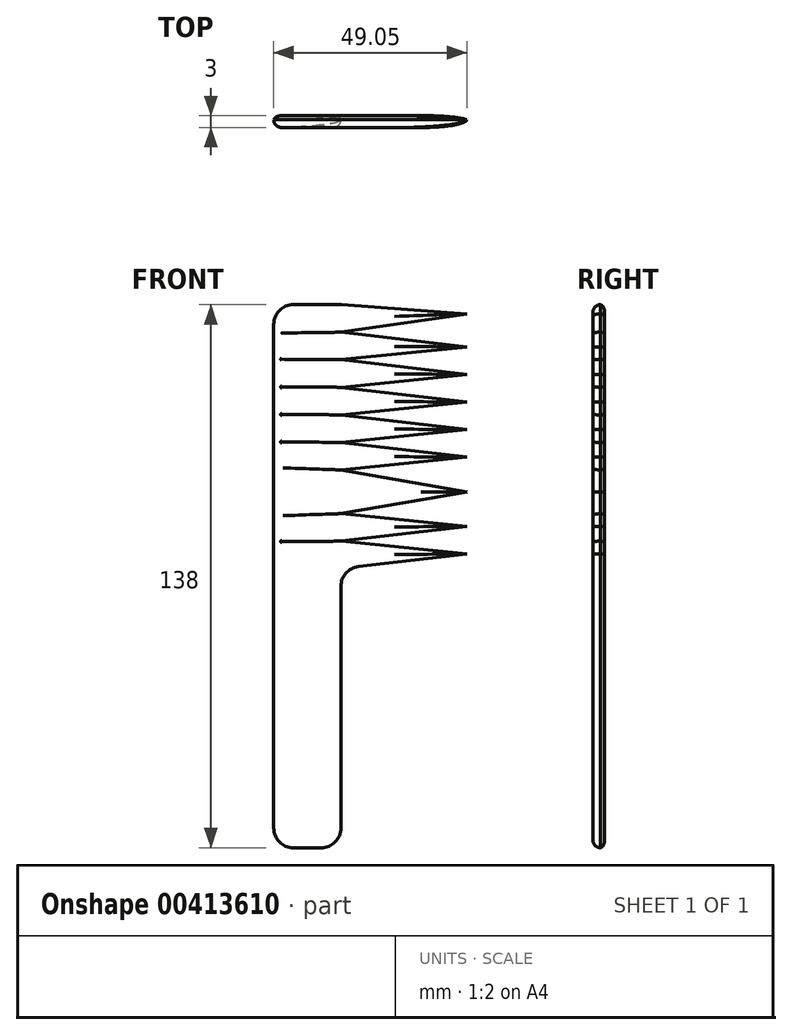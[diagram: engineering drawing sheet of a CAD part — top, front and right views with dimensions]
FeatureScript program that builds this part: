
annotation { "Feature Type Name" : "Feature", "Feature Type Description" : "" }
export const myFeature = defineFeature(function(context is Context, id is Id, definition is map)
    precondition{}
    {
        {
            var Q0;
            Q0=qCreatedBy(makeId("Front.planeOp"),FACE);
            var sketch = newSketch(context, id + "F0", { "sketchPlane" : qUnion([Q0])});
            skLineSegment(sketch, "E0", {"start": v(-43.23, 59.14) * mm, "end": v(-55.11, 59.14) * mm});
            skLineSegment(sketch, "E1", {"start": v(-60.11, 54.14) * mm, "end": v(-60.11, -73.86) * mm});
            skLineSegment(sketch, "E2", {"start": v(-55.11, -78.86) * mm, "end": v(-48.05, -78.86) * mm});
            skLineSegment(sketch, "E3", {"start": v(-43.05, -73.86) * mm, "end": v(-43.05, -12.4) * mm});
            skLineSegment(sketch, "E4", {"start": v(-11.06, 11.6) * mm, "end": v(-43.05, 17.14) * mm});
            skLineSegment(sketch, "E5", {"start": v(-43.05, 17.14) * mm, "end": v(-11.06, 20.38) * mm});
            skLineSegment(sketch, "E6", {"start": v(-11.06, 20.38) * mm, "end": v(-43.05, 24.14) * mm});
            skLineSegment(sketch, "E7", {"start": v(-43.05, 24.14) * mm, "end": v(-11.06, 27.38) * mm});
            skLineSegment(sketch, "E8", {"start": v(-11.06, 27.38) * mm, "end": v(-43.05, 31.14) * mm});
            skLineSegment(sketch, "E9", {"start": v(-43.05, 31.14) * mm, "end": v(-11.06, 34.38) * mm});
            skLineSegment(sketch, "E10", {"start": v(-11.06, 34.38) * mm, "end": v(-43.05, 38.14) * mm});
            skLineSegment(sketch, "E11", {"start": v(-43.05, 38.14) * mm, "end": v(-11.06, 41.38) * mm});
            skLineSegment(sketch, "E12", {"start": v(-11.06, 41.38) * mm, "end": v(-43.05, 45.14) * mm});
            skLineSegment(sketch, "E13", {"start": v(-43.05, 45.14) * mm, "end": v(-11.06, 48.38) * mm});
            skLineSegment(sketch, "E14", {"start": v(-11.06, 48.38) * mm, "end": v(-43.05, 52.14) * mm});
            skLineSegment(sketch, "E15", {"start": v(-43.05, 52.14) * mm, "end": v(-11.06, 56.81) * mm});
            skLineSegment(sketch, "E16", {"start": v(-11.06, 56.81) * mm, "end": v(-42.87, 59.13) * mm});
            skLineSegment(sketch, "E17.MirrorCS", {"start": v(-11.06, 11.6) * mm, "end": v(-43.05, 6.05) * mm});
            skLineSegment(sketch, "E18.MirrorCS", {"start": v(-11.06, 2.8) * mm, "end": v(-43.05, -0.95) * mm});
            skLineSegment(sketch, "E19.MirrorCS", {"start": v(-43.05, 6.05) * mm, "end": v(-11.06, 2.8) * mm});
            skLineSegment(sketch, "E20.MirrorCS", {"start": v(-43.05, -0.95) * mm, "end": v(-11.06, -4.2) * mm});
            skLineSegment(sketch, "E21.MirrorCS", {"start": v(-11.06, -4.2) * mm, "end": v(-38.63, -7.43) * mm});
            skPoint(sketch, "E22.visualSharp", {"position": v(-60.11, 59.14) * mm});
            skArc(sketch, "E22.filletArc", {"start": v(-55.11, 59.14) * mm, "mid": v(-58.65, 57.67) * mm, "end": v(-60.11, 54.14) * mm});
            skPoint(sketch, "E23.visualSharp", {"position": v(-60.11, -78.86) * mm});
            skArc(sketch, "E23.filletArc", {"start": v(-60.11, -73.86) * mm, "mid": v(-58.65, -77.4) * mm, "end": v(-55.11, -78.86) * mm});
            skPoint(sketch, "E24.visualSharp", {"position": v(-43.05, -78.86) * mm});
            skArc(sketch, "E24.filletArc", {"start": v(-48.05, -78.86) * mm, "mid": v(-44.51, -77.4) * mm, "end": v(-43.05, -73.86) * mm});
            skArc(sketch, "E25.filletArc", {"start": v(-38.63, -7.43) * mm, "mid": v(-41.79, -9.08) * mm, "end": v(-43.05, -12.4) * mm});
            skArc(sketch, "E26.filletArc", {"start": v(-42.87, 59.13) * mm, "mid": v(-43.05, 59.13) * mm, "end": v(-43.23, 59.14) * mm});
            skSolve(sketch);
        }
        {
            var Q0;
            Q0=makeQuery(id+"F0.imprint","IMPRINT",FACE,{"disambiguationData":[TD([[makeQuery(id+"F0.imprint","IMPRINT",EDGE,{"derivedFrom":sQuery(id+"F0.wireOp",EDGE,"E0")}),1.0]])]});
            extrude(context, id + "F1", {"entities" : qUnion([Q0]), "depth" : 3 * mm});
        }
        {
            var Q0;
            Q0=makeQuery(id+"F1.opExtrude","CAP_EDGE",EDGE,{"disambiguationData":[OSD([sQuery(id+"F0.wireOp",EDGE,"E1")])],"isStart":false});
            var Q1;
            Q1=makeQuery(id+"F1.opExtrude","CAP_EDGE",EDGE,{"disambiguationData":[OSD([sQuery(id+"F0.wireOp",EDGE,"E18.MirrorCS")])],"isStart":false});
            var Q2;
            Q2=makeQuery(id+"F1.opExtrude","CAP_EDGE",EDGE,{"disambiguationData":[OSD([sQuery(id+"F0.wireOp",EDGE,"E17.MirrorCS")])],"isStart":false});
            var Q3;
            Q3=makeQuery(id+"F1.opExtrude","CAP_EDGE",EDGE,{"disambiguationData":[OSD([sQuery(id+"F0.wireOp",EDGE,"E5")])],"isStart":false});
            var Q4;
            Q4=makeQuery(id+"F1.opExtrude","CAP_EDGE",EDGE,{"disambiguationData":[OSD([sQuery(id+"F0.wireOp",EDGE,"E7")])],"isStart":false});
            var Q5;
            Q5=makeQuery(id+"F1.opExtrude","CAP_EDGE",EDGE,{"disambiguationData":[OSD([sQuery(id+"F0.wireOp",EDGE,"E9")])],"isStart":false});
            var Q6;
            Q6=makeQuery(id+"F1.opExtrude","CAP_EDGE",EDGE,{"disambiguationData":[OSD([sQuery(id+"F0.wireOp",EDGE,"E11")])],"isStart":false});
            var Q7;
            Q7=makeQuery(id+"F1.opExtrude","CAP_EDGE",EDGE,{"disambiguationData":[OSD([sQuery(id+"F0.wireOp",EDGE,"E13")])],"isStart":false});
            var Q8;
            Q8=makeQuery(id+"F1.opExtrude","CAP_EDGE",EDGE,{"disambiguationData":[OSD([sQuery(id+"F0.wireOp",EDGE,"E15")])],"isStart":false});
            fillet(context, id + "F2", {"entities" : qUnion([Q0, Q1, Q2, Q3, Q4, Q5, Q6, Q7, Q8]), "radius" : 2 * mm, "tangentPropagation" : true, "allowEdgeOverflow" : false});
        }
        {
            var Q0;
            Q0=makeQuery(id+"F1.opExtrude","CAP_EDGE",EDGE,{"disambiguationData":[OSD([sQuery(id+"F0.wireOp",EDGE,"E1")])],"isStart":true});
            var Q1;
            Q1=makeQuery(id+"F1.opExtrude","CAP_EDGE",EDGE,{"disambiguationData":[OSD([sQuery(id+"F0.wireOp",EDGE,"E18.MirrorCS")])],"isStart":true});
            var Q2;
            Q2=makeQuery(id+"F1.opExtrude","CAP_EDGE",EDGE,{"disambiguationData":[OSD([sQuery(id+"F0.wireOp",EDGE,"E17.MirrorCS")])],"isStart":true});
            var Q3;
            Q3=makeQuery(id+"F1.opExtrude","CAP_EDGE",EDGE,{"disambiguationData":[OSD([sQuery(id+"F0.wireOp",EDGE,"E5")])],"isStart":true});
            var Q4;
            Q4=makeQuery(id+"F1.opExtrude","CAP_EDGE",EDGE,{"disambiguationData":[OSD([sQuery(id+"F0.wireOp",EDGE,"E7")])],"isStart":true});
            var Q5;
            Q5=makeQuery(id+"F1.opExtrude","CAP_EDGE",EDGE,{"disambiguationData":[OSD([sQuery(id+"F0.wireOp",EDGE,"E9")])],"isStart":true});
            var Q6;
            Q6=makeQuery(id+"F1.opExtrude","CAP_EDGE",EDGE,{"disambiguationData":[OSD([sQuery(id+"F0.wireOp",EDGE,"E11")])],"isStart":true});
            var Q7;
            Q7=makeQuery(id+"F1.opExtrude","CAP_EDGE",EDGE,{"disambiguationData":[OSD([sQuery(id+"F0.wireOp",EDGE,"E13")])],"isStart":true});
            var Q8;
            Q8=makeQuery(id+"F1.opExtrude","CAP_EDGE",EDGE,{"disambiguationData":[OSD([sQuery(id+"F0.wireOp",EDGE,"E15")])],"isStart":true});
            fillet(context, id + "F3", {"entities" : qUnion([Q0, Q1, Q2, Q3, Q4, Q5, Q6, Q7, Q8]), "radius" : 2 * mm, "tangentPropagation" : true, "allowEdgeOverflow" : false});
        }
        {
            var Q0;
            Q0=makeQuery(id+"F1.opExtrude","CAP_EDGE",EDGE,{"disambiguationData":[OSD([sQuery(id+"F0.wireOp",EDGE,"E10")])],"isStart":false});
            var Q1;
            Q1=makeQuery(id+"F1.opExtrude","CAP_EDGE",EDGE,{"disambiguationData":[OSD([sQuery(id+"F0.wireOp",EDGE,"E12")])],"isStart":false});
            var Q2;
            Q2=makeQuery(id+"F1.opExtrude","CAP_EDGE",EDGE,{"disambiguationData":[OSD([sQuery(id+"F0.wireOp",EDGE,"E14")])],"isStart":false});
            var Q3;
            Q3=makeQuery(id+"F1.opExtrude","CAP_EDGE",EDGE,{"disambiguationData":[OSD([sQuery(id+"F0.wireOp",EDGE,"E8")])],"isStart":false});
            var Q4;
            Q4=makeQuery(id+"F1.opExtrude","CAP_EDGE",EDGE,{"disambiguationData":[OSD([sQuery(id+"F0.wireOp",EDGE,"E6")])],"isStart":false});
            var Q5;
            Q5=makeQuery(id+"F1.opExtrude","CAP_EDGE",EDGE,{"disambiguationData":[OSD([sQuery(id+"F0.wireOp",EDGE,"E19.MirrorCS")])],"isStart":false});
            var Q6;
            Q6=makeQuery(id+"F1.opExtrude","CAP_EDGE",EDGE,{"disambiguationData":[OSD([sQuery(id+"F0.wireOp",EDGE,"E20.MirrorCS")])],"isStart":false});
            var Q7;
            Q7=makeQuery(id+"F1.opExtrude","CAP_EDGE",EDGE,{"disambiguationData":[OSD([sQuery(id+"F0.wireOp",EDGE,"E4")])],"isStart":false});
            fillet(context, id + "F4", {"entities" : qUnion([Q0, Q1, Q2, Q3, Q4, Q5, Q6, Q7]), "radius" : 2 * mm, "tangentPropagation" : true, "allowEdgeOverflow" : false});
        }
        {
            var Q0;
            Q0=makeQuery(id+"F1.opExtrude","CAP_EDGE",EDGE,{"disambiguationData":[OSD([sQuery(id+"F0.wireOp",EDGE,"E14")])],"isStart":true});
            var Q1;
            Q1=makeQuery(id+"F1.opExtrude","CAP_EDGE",EDGE,{"disambiguationData":[OSD([sQuery(id+"F0.wireOp",EDGE,"E12")])],"isStart":true});
            var Q2;
            Q2=makeQuery(id+"F1.opExtrude","CAP_EDGE",EDGE,{"disambiguationData":[OSD([sQuery(id+"F0.wireOp",EDGE,"E10")])],"isStart":true});
            var Q3;
            Q3=makeQuery(id+"F1.opExtrude","CAP_EDGE",EDGE,{"disambiguationData":[OSD([sQuery(id+"F0.wireOp",EDGE,"E8")])],"isStart":true});
            var Q4;
            Q4=makeQuery(id+"F1.opExtrude","CAP_EDGE",EDGE,{"disambiguationData":[OSD([sQuery(id+"F0.wireOp",EDGE,"E6")])],"isStart":true});
            var Q5;
            Q5=makeQuery(id+"F1.opExtrude","CAP_EDGE",EDGE,{"disambiguationData":[OSD([sQuery(id+"F0.wireOp",EDGE,"E4")])],"isStart":true});
            var Q6;
            Q6=makeQuery(id+"F1.opExtrude","CAP_EDGE",EDGE,{"disambiguationData":[OSD([sQuery(id+"F0.wireOp",EDGE,"E19.MirrorCS")])],"isStart":true});
            var Q7;
            Q7=makeQuery(id+"F1.opExtrude","CAP_EDGE",EDGE,{"disambiguationData":[OSD([sQuery(id+"F0.wireOp",EDGE,"E20.MirrorCS")])],"isStart":true});
            fillet(context, id + "F5", {"entities" : qUnion([Q0, Q1, Q2, Q3, Q4, Q5, Q6, Q7]), "radius" : 2 * mm, "tangentPropagation" : true, "allowEdgeOverflow" : false});
        }
    });
